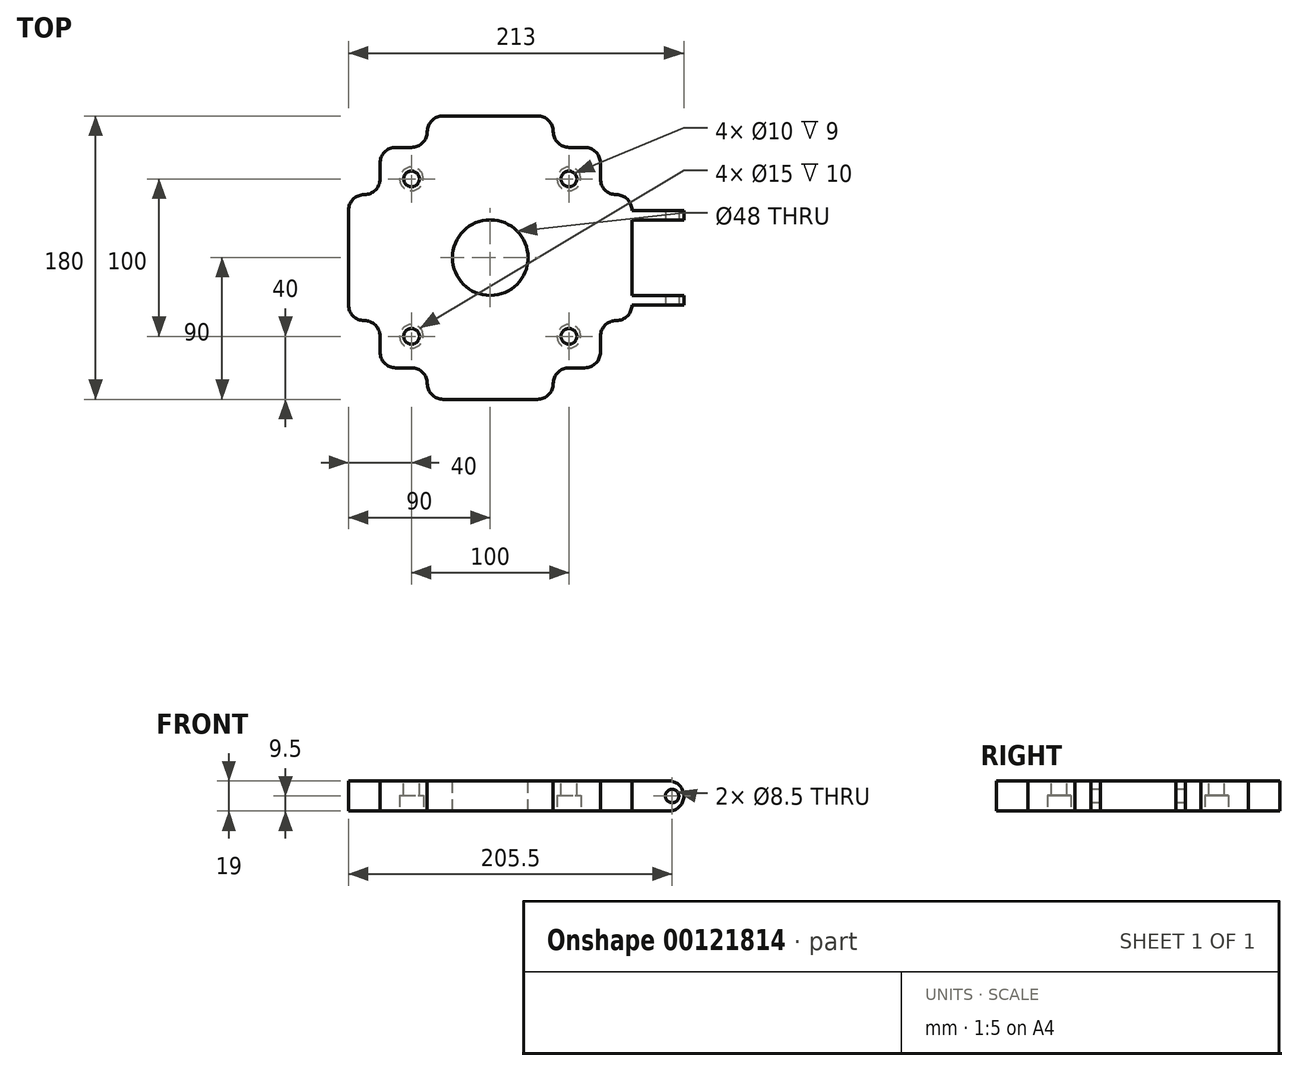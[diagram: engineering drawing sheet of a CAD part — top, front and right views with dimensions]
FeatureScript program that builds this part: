
annotation { "Feature Type Name" : "Feature", "Feature Type Description" : "" }
export const myFeature = defineFeature(function(context is Context, id is Id, definition is map)
    precondition{}
    {
        {
            var Q0;
            Q0=qCreatedBy(makeId("Top.planeOp"),FACE);
            var sketch = newSketch(context, id + "F0", { "sketchPlane" : qUnion([Q0])});
            skPoint(sketch, "E0.middle", {"position": v(0, 0) * mm});
            skLineSegment(sketch, "E1", {"start": v(-40, 90) * mm, "end": v(-40, 70) * mm});
            skLineSegment(sketch, "E2", {"start": v(-40, 70) * mm, "end": v(-70, 70) * mm});
            skLineSegment(sketch, "E3", {"start": v(-70, 70) * mm, "end": v(-70, 40) * mm});
            skLineSegment(sketch, "E4", {"start": v(-70, 40) * mm, "end": v(-90, 40) * mm});
            skLineSegment(sketch, "E5", {"start": v(-90, -40) * mm, "end": v(-70, -40) * mm});
            skLineSegment(sketch, "E6", {"start": v(-70, -40) * mm, "end": v(-70, -70) * mm});
            skLineSegment(sketch, "E7", {"start": v(-70, -70) * mm, "end": v(-40, -70) * mm});
            skLineSegment(sketch, "E8", {"start": v(-40, -70) * mm, "end": v(-40, -90) * mm});
            skLineSegment(sketch, "E9", {"start": v(40, -90) * mm, "end": v(40, -70) * mm});
            skLineSegment(sketch, "E10", {"start": v(40, -70) * mm, "end": v(70, -70) * mm});
            skLineSegment(sketch, "E11", {"start": v(70, -70) * mm, "end": v(70, -40) * mm});
            skLineSegment(sketch, "E12", {"start": v(70, -40) * mm, "end": v(90, -40) * mm});
            skLineSegment(sketch, "E13", {"start": v(40, 90) * mm, "end": v(40, 70) * mm});
            skLineSegment(sketch, "E14", {"start": v(40, 70) * mm, "end": v(70, 70) * mm});
            skLineSegment(sketch, "E15", {"start": v(70, 70) * mm, "end": v(70, 40) * mm});
            skLineSegment(sketch, "E16", {"start": v(70, 40) * mm, "end": v(90, 40) * mm});
            skLineSegment(sketch, "E17", {"start": v(-40, 90) * mm, "end": v(40, 90) * mm});
            skLineSegment(sketch, "E18", {"start": v(-90, 40) * mm, "end": v(-90, -40) * mm});
            skLineSegment(sketch, "E19", {"start": v(-40, -90) * mm, "end": v(40, -90) * mm});
            skLineSegment(sketch, "E20", {"start": v(90, -40) * mm, "end": v(90, 40) * mm});
            skLineSegment(sketch, "E21", {"start": v(90, 0) * mm, "end": v(-98.72, 0) * mm});
            skPoint(sketch, "E21.endSnap0", {"position": v(-90, 0) * mm});
            skLineSegment(sketch, "E22", {"start": v(0, -90) * mm, "end": v(0, 103.29) * mm});
            skSolve(sketch);
        }
        {
            var Q0;
            Q0 = qSketchRegion(id + "F0", true);
            extrude(context, id + "F1", {"entities" : qUnion([Q0]), "depth" : 19 * mm});
        }
        {
            var Q0;
            Q0=makeQuery(id+"F1.opExtrude","CAP_FACE",FACE,{"disambiguationData":[OSD([sQuery(id+"F0.wireOp",EDGE,"E1"),sQuery(id+"F0.wireOp",EDGE,"E2"),sQuery(id+"F0.wireOp",EDGE,"E3"),sQuery(id+"F0.wireOp",EDGE,"E4"),sQuery(id+"F0.wireOp",EDGE,"E5"),sQuery(id+"F0.wireOp",EDGE,"E6"),sQuery(id+"F0.wireOp",EDGE,"E7"),sQuery(id+"F0.wireOp",EDGE,"E8"),sQuery(id+"F0.wireOp",EDGE,"E9"),sQuery(id+"F0.wireOp",EDGE,"E10"),sQuery(id+"F0.wireOp",EDGE,"E11"),sQuery(id+"F0.wireOp",EDGE,"E12"),sQuery(id+"F0.wireOp",EDGE,"E13"),sQuery(id+"F0.wireOp",EDGE,"E14"),sQuery(id+"F0.wireOp",EDGE,"E15"),sQuery(id+"F0.wireOp",EDGE,"E16"),sQuery(id+"F0.wireOp",EDGE,"E17"),sQuery(id+"F0.wireOp",EDGE,"E18"),sQuery(id+"F0.wireOp",EDGE,"E19"),sQuery(id+"F0.wireOp",EDGE,"E20")])],"isStart":false});
            var sketch = newSketch(context, id + "F2", { "sketchPlane" : qUnion([Q0])});
            skCircle(sketch, "E23", {"center": v(0, 0) * mm, "radius": 24 * mm});
            skSolve(sketch);
        }
        {
            var Q0;
            Q0 = qSketchRegion(id + "F2", true);
            extrude(context, id + "F3", {"entities" : qUnion([Q0]), "operationType" : NewBodyOperationType.REMOVE, "oppositeDirection" : true, "depth" : 25 * mm});
        }
        {
            var Q0;
            Q0=makeQuery(id+"F1.opExtrude","SWEPT_EDGE",EDGE,{"disambiguationData":[OSD([sQuery(id+"F0.wireOp",EDGE,"E3"),sQuery(id+"F0.wireOp",EDGE,"E4")])]});
            var Q1;
            Q1=makeQuery(id+"F1.opExtrude","SWEPT_EDGE",EDGE,{"disambiguationData":[OSD([sQuery(id+"F0.wireOp",EDGE,"E1"),sQuery(id+"F0.wireOp",EDGE,"E2")])]});
            var Q2;
            Q2=makeQuery(id+"F1.opExtrude","SWEPT_EDGE",EDGE,{"disambiguationData":[OSD([sQuery(id+"F0.wireOp",EDGE,"E1"),sQuery(id+"F0.wireOp",EDGE,"E17")])]});
            var Q3;
            Q3=makeQuery(id+"F1.opExtrude","SWEPT_EDGE",EDGE,{"disambiguationData":[OSD([sQuery(id+"F0.wireOp",EDGE,"E2"),sQuery(id+"F0.wireOp",EDGE,"E3")])]});
            var Q4;
            Q4=makeQuery(id+"F1.opExtrude","SWEPT_EDGE",EDGE,{"disambiguationData":[OSD([sQuery(id+"F0.wireOp",EDGE,"E4"),sQuery(id+"F0.wireOp",EDGE,"E18")])]});
            var Q5;
            Q5=makeQuery(id+"F1.opExtrude","SWEPT_EDGE",EDGE,{"disambiguationData":[OSD([sQuery(id+"F0.wireOp",EDGE,"E8"),sQuery(id+"F0.wireOp",EDGE,"E19")])]});
            var Q6;
            Q6=makeQuery(id+"F1.opExtrude","SWEPT_EDGE",EDGE,{"disambiguationData":[OSD([sQuery(id+"F0.wireOp",EDGE,"E7"),sQuery(id+"F0.wireOp",EDGE,"E8")])]});
            var Q7;
            Q7=makeQuery(id+"F1.opExtrude","SWEPT_EDGE",EDGE,{"disambiguationData":[OSD([sQuery(id+"F0.wireOp",EDGE,"E6"),sQuery(id+"F0.wireOp",EDGE,"E7")])]});
            var Q8;
            Q8=makeQuery(id+"F1.opExtrude","SWEPT_EDGE",EDGE,{"disambiguationData":[OSD([sQuery(id+"F0.wireOp",EDGE,"E5"),sQuery(id+"F0.wireOp",EDGE,"E6")])]});
            var Q9;
            Q9=makeQuery(id+"F1.opExtrude","SWEPT_EDGE",EDGE,{"disambiguationData":[OSD([sQuery(id+"F0.wireOp",EDGE,"E5"),sQuery(id+"F0.wireOp",EDGE,"E18")])]});
            var Q10;
            Q10=makeQuery(id+"F1.opExtrude","SWEPT_EDGE",EDGE,{"disambiguationData":[OSD([sQuery(id+"F0.wireOp",EDGE,"E9"),sQuery(id+"F0.wireOp",EDGE,"E19")])]});
            var Q11;
            Q11=makeQuery(id+"F1.opExtrude","SWEPT_EDGE",EDGE,{"disambiguationData":[OSD([sQuery(id+"F0.wireOp",EDGE,"E9"),sQuery(id+"F0.wireOp",EDGE,"E10")])]});
            var Q12;
            Q12=makeQuery(id+"F1.opExtrude","SWEPT_EDGE",EDGE,{"disambiguationData":[OSD([sQuery(id+"F0.wireOp",EDGE,"E10"),sQuery(id+"F0.wireOp",EDGE,"E11")])]});
            var Q13;
            Q13=makeQuery(id+"F1.opExtrude","SWEPT_EDGE",EDGE,{"disambiguationData":[OSD([sQuery(id+"F0.wireOp",EDGE,"E11"),sQuery(id+"F0.wireOp",EDGE,"E12")])]});
            var Q14;
            Q14=makeQuery(id+"F1.opExtrude","SWEPT_EDGE",EDGE,{"disambiguationData":[OSD([sQuery(id+"F0.wireOp",EDGE,"E12"),sQuery(id+"F0.wireOp",EDGE,"E20")])]});
            var Q15;
            Q15=makeQuery(id+"F1.opExtrude","SWEPT_EDGE",EDGE,{"disambiguationData":[OSD([sQuery(id+"F0.wireOp",EDGE,"E16"),sQuery(id+"F0.wireOp",EDGE,"E20")])]});
            var Q16;
            Q16=makeQuery(id+"F1.opExtrude","SWEPT_EDGE",EDGE,{"disambiguationData":[OSD([sQuery(id+"F0.wireOp",EDGE,"E15"),sQuery(id+"F0.wireOp",EDGE,"E16")])]});
            var Q17;
            Q17=makeQuery(id+"F1.opExtrude","SWEPT_EDGE",EDGE,{"disambiguationData":[OSD([sQuery(id+"F0.wireOp",EDGE,"E14"),sQuery(id+"F0.wireOp",EDGE,"E15")])]});
            var Q18;
            Q18=makeQuery(id+"F1.opExtrude","SWEPT_EDGE",EDGE,{"disambiguationData":[OSD([sQuery(id+"F0.wireOp",EDGE,"E13"),sQuery(id+"F0.wireOp",EDGE,"E14")])]});
            var Q19;
            Q19=makeQuery(id+"F1.opExtrude","SWEPT_EDGE",EDGE,{"disambiguationData":[OSD([sQuery(id+"F0.wireOp",EDGE,"E13"),sQuery(id+"F0.wireOp",EDGE,"E17")])]});
            fillet(context, id + "F4", {"entities" : qUnion([Q0, Q1, Q2, Q3, Q4, Q5, Q6, Q7, Q8, Q9, Q10, Q11, Q12, Q13, Q14, Q15, Q16, Q17, Q18, Q19]), "radius" : 10 * mm, "tangentPropagation" : true, "allowEdgeOverflow" : false});
        }
        {
            var Q0;
            Q0=makeQuery(id+"F1.opExtrude","CAP_FACE",FACE,{"disambiguationData":[OSD([sQuery(id+"F0.wireOp",EDGE,"E1"),sQuery(id+"F0.wireOp",EDGE,"E2"),sQuery(id+"F0.wireOp",EDGE,"E3"),sQuery(id+"F0.wireOp",EDGE,"E4"),sQuery(id+"F0.wireOp",EDGE,"E5"),sQuery(id+"F0.wireOp",EDGE,"E6"),sQuery(id+"F0.wireOp",EDGE,"E7"),sQuery(id+"F0.wireOp",EDGE,"E8"),sQuery(id+"F0.wireOp",EDGE,"E9"),sQuery(id+"F0.wireOp",EDGE,"E10"),sQuery(id+"F0.wireOp",EDGE,"E11"),sQuery(id+"F0.wireOp",EDGE,"E12"),sQuery(id+"F0.wireOp",EDGE,"E13"),sQuery(id+"F0.wireOp",EDGE,"E14"),sQuery(id+"F0.wireOp",EDGE,"E15"),sQuery(id+"F0.wireOp",EDGE,"E16"),sQuery(id+"F0.wireOp",EDGE,"E17"),sQuery(id+"F0.wireOp",EDGE,"E18"),sQuery(id+"F0.wireOp",EDGE,"E19"),sQuery(id+"F0.wireOp",EDGE,"E20")])],"isStart":false});
            var sketch = newSketch(context, id + "F5", { "sketchPlane" : qUnion([Q0])});
            skPoint(sketch, "E24.middle", {"position": v(0, 0) * mm});
            skCircle(sketch, "E25", {"center": v(-50, -50) * mm, "radius": 5 * mm});
            skCircle(sketch, "E26", {"center": v(50, -50) * mm, "radius": 5 * mm});
            skCircle(sketch, "E27", {"center": v(50, 50) * mm, "radius": 5 * mm});
            skCircle(sketch, "E28", {"center": v(-50, 50) * mm, "radius": 5 * mm});
            skSolve(sketch);
        }
        {
            var Q0;
            Q0=makeQuery(id+"F5.imprint","IMPRINT",FACE,{"disambiguationData":[TD([[makeQuery(id+"F5.imprint","IMPRINT",EDGE,{"derivedFrom":sQuery(id+"F5.wireOp",EDGE,"E25")}),1.0]])]});
            var Q1;
            Q1=makeQuery(id+"F5.imprint","IMPRINT",FACE,{"disambiguationData":[TD([[makeQuery(id+"F5.imprint","IMPRINT",EDGE,{"derivedFrom":sQuery(id+"F5.wireOp",EDGE,"E26")}),1.0]])]});
            var Q2;
            Q2=makeQuery(id+"F5.imprint","IMPRINT",FACE,{"disambiguationData":[TD([[makeQuery(id+"F5.imprint","IMPRINT",EDGE,{"derivedFrom":sQuery(id+"F5.wireOp",EDGE,"E28")}),1.0]])]});
            var Q3;
            Q3=makeQuery(id+"F5.imprint","IMPRINT",FACE,{"disambiguationData":[TD([[makeQuery(id+"F5.imprint","IMPRINT",EDGE,{"derivedFrom":sQuery(id+"F5.wireOp",EDGE,"E27")}),1.0]])]});
            extrude(context, id + "F6", {"entities" : qUnion([Q0, Q1, Q2, Q3]), "operationType" : NewBodyOperationType.REMOVE, "oppositeDirection" : true, "depth" : 25 * mm});
        }
        {
            var Q0;
            Q0=makeQuery(id+"F1.opExtrude","CAP_FACE",FACE,{"disambiguationData":[OSD([sQuery(id+"F0.wireOp",EDGE,"E1"),sQuery(id+"F0.wireOp",EDGE,"E2"),sQuery(id+"F0.wireOp",EDGE,"E3"),sQuery(id+"F0.wireOp",EDGE,"E4"),sQuery(id+"F0.wireOp",EDGE,"E5"),sQuery(id+"F0.wireOp",EDGE,"E6"),sQuery(id+"F0.wireOp",EDGE,"E7"),sQuery(id+"F0.wireOp",EDGE,"E8"),sQuery(id+"F0.wireOp",EDGE,"E9"),sQuery(id+"F0.wireOp",EDGE,"E10"),sQuery(id+"F0.wireOp",EDGE,"E11"),sQuery(id+"F0.wireOp",EDGE,"E12"),sQuery(id+"F0.wireOp",EDGE,"E13"),sQuery(id+"F0.wireOp",EDGE,"E14"),sQuery(id+"F0.wireOp",EDGE,"E15"),sQuery(id+"F0.wireOp",EDGE,"E16"),sQuery(id+"F0.wireOp",EDGE,"E17"),sQuery(id+"F0.wireOp",EDGE,"E18"),sQuery(id+"F0.wireOp",EDGE,"E19"),sQuery(id+"F0.wireOp",EDGE,"E20")])],"isStart":true});
            var sketch = newSketch(context, id + "F7", { "sketchPlane" : qUnion([Q0])});
            skCircle(sketch, "E29", {"center": v(-50, 50) * mm, "radius": 7.5 * mm});
            skCircle(sketch, "E30", {"center": v(50, 50) * mm, "radius": 7.5 * mm});
            skCircle(sketch, "E31", {"center": v(-50, -50) * mm, "radius": 7.5 * mm});
            skCircle(sketch, "E32", {"center": v(50, -50) * mm, "radius": 7.5 * mm});
            skSolve(sketch);
        }
        {
            var Q0;
            Q0 = qSketchRegion(id + "F7", true);
            extrude(context, id + "F8", {"entities" : qUnion([Q0]), "operationType" : NewBodyOperationType.REMOVE, "oppositeDirection" : true, "depth" : 10 * mm});
        }
        {
            var Q0;
            Q0=makeQuery(id+"F1.opExtrude","SWEPT_FACE",FACE,{"disambiguationData":[OSD([sQuery(id+"F0.wireOp",EDGE,"E20")])]});
            var sketch = newSketch(context, id + "F9", { "sketchPlane" : qUnion([Q0])});
            skPoint(sketch, "E33.middle", {"position": v(-0.9, 9.35) * mm});
            skLineSegment(sketch, "E34", {"start": v(-30, 19) * mm, "end": v(-24, 19) * mm});
            skLineSegment(sketch, "E35", {"start": v(-24, 19) * mm, "end": v(-24, 0) * mm});
            skLineSegment(sketch, "E36", {"start": v(-24, 0) * mm, "end": v(-30, 0) * mm});
            skLineSegment(sketch, "E37", {"start": v(-30, 0) * mm, "end": v(-30, 19) * mm});
            skLineSegment(sketch, "E38", {"start": v(30, 0) * mm, "end": v(24, 0) * mm});
            skLineSegment(sketch, "E39", {"start": v(24, 0) * mm, "end": v(24, 19) * mm});
            skLineSegment(sketch, "E40", {"start": v(24, 19) * mm, "end": v(30, 19) * mm});
            skLineSegment(sketch, "E41", {"start": v(30, 19) * mm, "end": v(30, 0) * mm});
            skSolve(sketch);
        }
        {
            var Q0;
            Q0 = qSketchRegion(id + "F9", true);
            extrude(context, id + "F10", {"entities" : qUnion([Q0]), "operationType" : NewBodyOperationType.ADD, "depth" : 25 * mm});
        }
        {
            var Q0;
            Q0 = qSketchRegion(id + "F9", true);
            extrude(context, id + "F11", {"entities" : qUnion([Q0]), "operationType" : NewBodyOperationType.ADD, "depth" : 25 * mm});
        }
        {
            var Q0;
            Q0=makeQuery(id+"F10.opExtrude","SWEPT_FACE",FACE,{"disambiguationData":[OSD([sQuery(id+"F9.wireOp",EDGE,"E37")])]});
            var sketch = newSketch(context, id + "F12", { "sketchPlane" : qUnion([Q0])});
            skArc(sketch, "E42", {"start": v(125, 19) * mm, "mid": v(134.5, 9.5) * mm, "end": v(125, 0) * mm});
            skLineSegment(sketch, "E43", {"start": v(115, 0) * mm, "end": v(125, 0) * mm});
            skLineSegment(sketch, "E44", {"start": v(125, 19) * mm, "end": v(115, 19) * mm});
            skCircle(sketch, "E45", {"center": v(125, 9.5) * mm, "radius": 4.25 * mm});
            skSolve(sketch);
        }
        {
            var Q0;
            Q0 = qSketchRegion(id + "F12", true);
            var Q1;
            {var subQ4=sQuery(id+"F12.wireOp",EDGE,"E44");Q1=makeQuery(id+"F12.imprint","IMPRINT",FACE,{"disambiguationData":[TD([[makeQuery(id+"F12.imprint","IMPRINT",EDGE,{"derivedFrom":subQ4}),1.0]])]});}
            extrude(context, id + "F13", {"entities" : qUnion([Q0, Q1]), "operationType" : NewBodyOperationType.REMOVE, "oppositeDirection" : true, "depth" : 250 * mm});
        }
        {
            var Q0;
            Q0=makeQuery(id+"F10.opExtrude","SWEPT_FACE",FACE,{"disambiguationData":[OSD([sQuery(id+"F9.wireOp",EDGE,"E37")])]});
            var sketch = newSketch(context, id + "F14", { "sketchPlane" : qUnion([Q0])});
            skCircle(sketch, "E46", {"center": v(110.7, 9.5) * mm, "radius": 4.12 * mm});
            skSolve(sketch);
        }
        {
            var Q0;
            Q0=makeQuery(id+"F10.opExtrude","CAP_FACE",FACE,{"disambiguationData":[OSD([sQuery(id+"F9.wireOp",EDGE,"E34"),sQuery(id+"F9.wireOp",EDGE,"E35"),sQuery(id+"F9.wireOp",EDGE,"E36"),sQuery(id+"F9.wireOp",EDGE,"E37")])],"isStart":false});
            var Q1;
            Q1=makeQuery(id+"F10.opExtrude","CAP_FACE",FACE,{"disambiguationData":[OSD([sQuery(id+"F9.wireOp",EDGE,"E38"),sQuery(id+"F9.wireOp",EDGE,"E39"),sQuery(id+"F9.wireOp",EDGE,"E40"),sQuery(id+"F9.wireOp",EDGE,"E41")])],"isStart":false});
            extrude(context, id + "F15", {"entities" : qUnion([Q0, Q1]), "operationType" : NewBodyOperationType.ADD, "depth" : 8 * mm});
        }
        {
            var Q0;
            {var subQ0=sQuery(id+"F9.wireOp",EDGE,"E37");Q0=makeQuery(id+"F15.boolean.opBoolean","MERGE",FACE,{"derivedFrom":[makeQuery(id+"F10.opExtrude","SWEPT_FACE",FACE,{"disambiguationData":[OSD([subQ0])]}),makeQuery(id+"F15.opExtrude","SWEPT_FACE",FACE,{"disambiguationData":[OSD([subQ0])]})]});}
            var sketch = newSketch(context, id + "F16", { "sketchPlane" : qUnion([Q0])});
            skPoint(sketch, "E47.endSnap0", {"position": v(123, 9.5) * mm});
            skCircle(sketch, "E48", {"center": v(115.5, 9.5) * mm, "radius": 4.25 * mm});
            skSolve(sketch);
        }
        {
            var Q0;
            Q0 = qSketchRegion(id + "F16", true);
            extrude(context, id + "F17", {"entities" : qUnion([Q0]), "operationType" : NewBodyOperationType.REMOVE, "oppositeDirection" : true, "depth" : 250 * mm});
        }
        {
            var Q0;
            Q0=makeQuery(id+"F15.opExtrude","CAP_EDGE",EDGE,{"disambiguationData":[OSD([sQuery(id+"F9.wireOp",EDGE,"E38")])],"isStart":false});
            var Q1;
            Q1=makeQuery(id+"F15.opExtrude","CAP_EDGE",EDGE,{"disambiguationData":[OSD([sQuery(id+"F9.wireOp",EDGE,"E36")])],"isStart":false});
            var Q2;
            Q2=makeQuery(id+"F15.opExtrude","CAP_EDGE",EDGE,{"disambiguationData":[OSD([sQuery(id+"F9.wireOp",EDGE,"E34")])],"isStart":false});
            var Q3;
            Q3=makeQuery(id+"F15.opExtrude","CAP_EDGE",EDGE,{"disambiguationData":[OSD([sQuery(id+"F9.wireOp",EDGE,"E40")])],"isStart":false});
            fillet(context, id + "F18", {"entities" : qUnion([Q0, Q1, Q2, Q3]), "radius" : 9.5 * mm, "tangentPropagation" : true, "allowEdgeOverflow" : false});
        }
    });
